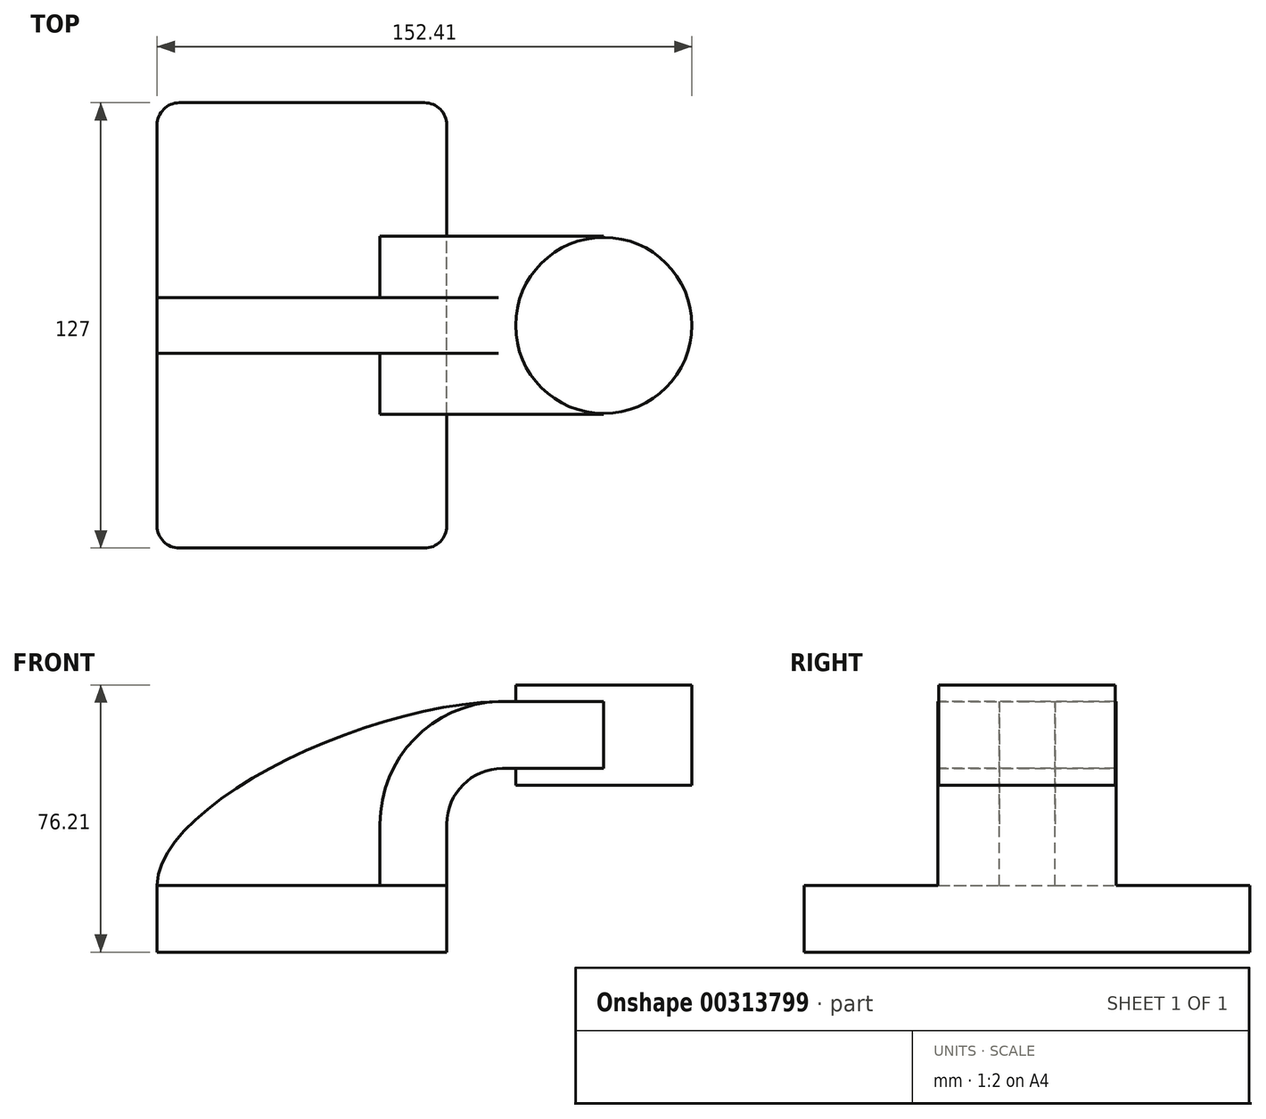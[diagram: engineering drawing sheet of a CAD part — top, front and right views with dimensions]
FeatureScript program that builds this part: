
annotation { "Feature Type Name" : "Feature", "Feature Type Description" : "" }
export const myFeature = defineFeature(function(context is Context, id is Id, definition is map)
    precondition{}
    {
        {
            var Q0;
            Q0=qCreatedBy(makeId("Front.planeOp"),FACE);
            var sketch = newSketch(context, id + "F0", { "sketchPlane" : qUnion([Q0])});
            skLineSegment(sketch, "E0.bottom", {"start": v(-41.28, -9.53) * mm, "end": v(41.28, -9.53) * mm});
            skLineSegment(sketch, "E0.top", {"start": v(-41.28, 9.53) * mm, "end": v(41.28, 9.53) * mm});
            skLineSegment(sketch, "E0.left", {"start": v(-41.28, -9.53) * mm, "end": v(-41.28, 9.53) * mm});
            skLineSegment(sketch, "E0.right", {"start": v(41.28, -9.53) * mm, "end": v(41.28, 9.52) * mm});
            skPoint(sketch, "E0.middle", {"position": v(0, 0) * mm});
            skLineSegment(sketch, "E1.bottom", {"start": v(111.12, 38.1) * mm, "end": v(60.32, 38.1) * mm});
            skLineSegment(sketch, "E1.top", {"start": v(111.12, 66.68) * mm, "end": v(60.32, 66.68) * mm});
            skLineSegment(sketch, "E1.left", {"start": v(111.12, 38.1) * mm, "end": v(111.12, 66.68) * mm});
            skLineSegment(sketch, "E1.right", {"start": v(60.32, 38.1) * mm, "end": v(60.32, 66.68) * mm});
            skPoint(sketch, "E1.middle", {"position": v(85.72, 52.39) * mm});
            skLineSegment(sketch, "E2", {"start": v(41.28, 9.52) * mm, "end": v(41.28, 26.99) * mm});
            skArc(sketch, "E3", {"start": v(41.27, 26.99) * mm, "mid": v(45.92, 38.21) * mm, "end": v(57.15, 42.86) * mm});
            skLineSegment(sketch, "E4", {"start": v(57.15, 42.86) * mm, "end": v(86, 42.86) * mm});
            skLineSegment(sketch, "E5.0", {"start": v(57.15, 61.91) * mm, "end": v(86, 61.91) * mm});
            skArc(sketch, "E5.1", {"start": v(22.23, 26.99) * mm, "mid": v(32.45, 51.68) * mm, "end": v(57.15, 61.91) * mm});
            skLineSegment(sketch, "E5.2", {"start": v(22.22, 9.52) * mm, "end": v(22.22, 26.99) * mm});
            skLineSegment(sketch, "E6", {"start": v(86, 38.1) * mm, "end": v(86, 66.68) * mm});
            skPoint(sketch, "E6.startSnap0", {"position": v(85.72, 38.1) * mm});
            skFitSpline(sketch, "E7", {"points": [v(-41.28, 9.53) * mm, v(57.15, 61.91) * mm], "startDerivative": vector(1.27, 70.62) * mm, "endDerivative": vector(113.86, 1.05) * mm});
            skSolve(sketch);
        }
        {
            var Q0;
            Q0=makeQuery(id+"F0.imprint","IMPRINT",FACE,{"disambiguationData":[TD([[makeQuery(id+"F0.imprint","IMPRINT",EDGE,{"derivedFrom":sQuery(id+"F0.wireOp",EDGE,"E0.bottom")}),1.0]])]});
            extrude(context, id + "F1", {"entities" : qUnion([Q0]), "depth" : 127 * mm, "symmetric" : true});
        }
        {
            var Q0;
            {var subQ1=sQuery(id+"F0.wireOp",EDGE,"E2");Q0=makeQuery(id+"F0.imprint","IMPRINT",FACE,{"disambiguationData":[TD([[makeQuery(id+"F0.imprint","IMPRINT",EDGE,{"derivedFrom":subQ1}),1.0]])]});}
            var Q1;
            {var subQ0=sQuery(id+"F0.wireOp",EDGE,"E4");var subQ1=sQuery(id+"F0.wireOp",EDGE,"E1.right");var subQ2=makeQuery(id+"F0.imprint","INTERSECT",VERTEX,{"derivedFrom":[subQ1,subQ0]});Q1=makeQuery(id+"F0.imprint","IMPRINT",FACE,{"disambiguationData":[TD([[makeQuery(id+"F0.imprint","IMPRINT",EDGE,{"disambiguationData":[TD([[subQ2,-1.0]])],"derivedFrom":subQ1}),-1.0]])]});}
            extrude(context, id + "F2", {"entities" : qUnion([Q0, Q1]), "operationType" : NewBodyOperationType.ADD, "depth" : 50.8 * mm, "symmetric" : true});
        }
        {
            var Q0;
            {var subQ3=sQuery(id+"F0.wireOp",EDGE,"E5.2");Q0=makeQuery(id+"F0.imprint","IMPRINT",FACE,{"disambiguationData":[TD([[makeQuery(id+"F0.imprint","IMPRINT",EDGE,{"derivedFrom":subQ3}),1.0]])]});}
            extrude(context, id + "F3", {"entities" : qUnion([Q0]), "operationType" : NewBodyOperationType.ADD, "depth" : 15.88 * mm, "symmetric" : true});
        }
        {
            var Q0;
            {var subQ0=sQuery(id+"F0.wireOp",EDGE,"E1.left");Q0=makeQuery(id+"F0.imprint","IMPRINT",FACE,{"disambiguationData":[TD([[makeQuery(id+"F0.imprint","IMPRINT",EDGE,{"derivedFrom":subQ0}),1.0]])]});}
            var Q1;
            Q1=sQuery(id+"F0.wireOp",EDGE,"E6");
            revolve(context, id + "F4", {"operationType" : NewBodyOperationType.ADD, "entities" : qUnion([Q0]), "axis" : qUnion([Q1]), "revolveType" : RevolveType.FULL});
        }
        {
            var Q0;
            Q0=makeQuery(id+"F1.opExtrude","CAP_EDGE",EDGE,{"disambiguationData":[OSD([sQuery(id+"F0.wireOp",EDGE,"E0.left")])],"isStart":false});
            var Q1;
            Q1=makeQuery(id+"F1.opExtrude","CAP_EDGE",EDGE,{"disambiguationData":[OSD([sQuery(id+"F0.wireOp",EDGE,"E0.right")])],"isStart":false});
            var Q2;
            Q2=makeQuery(id+"F1.opExtrude","CAP_EDGE",EDGE,{"disambiguationData":[OSD([sQuery(id+"F0.wireOp",EDGE,"E0.right")])],"isStart":true});
            var Q3;
            Q3=makeQuery(id+"F1.opExtrude","CAP_EDGE",EDGE,{"disambiguationData":[OSD([sQuery(id+"F0.wireOp",EDGE,"E0.left")])],"isStart":true});
            fillet(context, id + "F5", {"entities" : qUnion([Q0, Q1, Q2, Q3]), "radius" : 6.35 * mm, "tangentPropagation" : true, "allowEdgeOverflow" : false});
        }
    });
